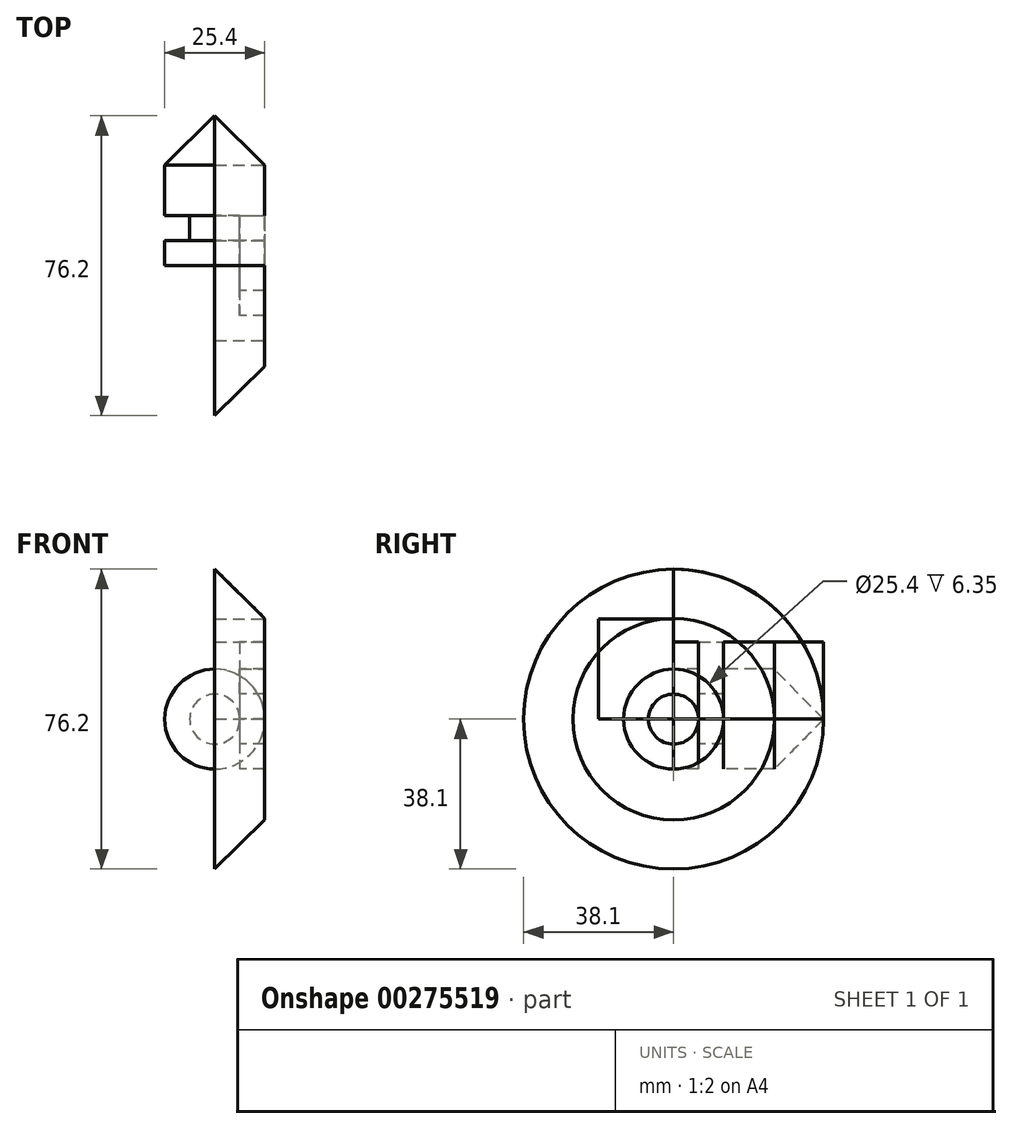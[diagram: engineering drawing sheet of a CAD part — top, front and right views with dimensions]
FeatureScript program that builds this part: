
annotation { "Feature Type Name" : "Feature", "Feature Type Description" : "" }
export const myFeature = defineFeature(function(context is Context, id is Id, definition is map)
    precondition{}
    {
        {
            var Q0;
            Q0=qCreatedBy(makeId("Top.planeOp"),FACE);
            var sketch = newSketch(context, id + "F0", { "sketchPlane" : qUnion([Q0])});
            skLineSegment(sketch, "E0", {"start": v(0, 0) * mm, "end": v(0, 38.1) * mm});
            skLineSegment(sketch, "E1", {"start": v(0, 0) * mm, "end": v(12.7, 0) * mm});
            skLineSegment(sketch, "E2", {"start": v(12.7, 0) * mm, "end": v(12.7, 6.35) * mm});
            skLineSegment(sketch, "E3", {"start": v(12.7, 6.35) * mm, "end": v(6.35, 6.35) * mm});
            skLineSegment(sketch, "E4", {"start": v(6.35, 6.35) * mm, "end": v(6.35, 12.7) * mm});
            skLineSegment(sketch, "E5", {"start": v(6.35, 12.7) * mm, "end": v(12.7, 12.7) * mm});
            skLineSegment(sketch, "E6", {"start": v(12.7, 12.7) * mm, "end": v(12.7, 25.6) * mm});
            skLineSegment(sketch, "E7", {"start": v(12.7, 25.6) * mm, "end": v(0, 38.1) * mm});
            skSolve(sketch);
        }
        {
            var Q0;
            Q0=makeQuery(id+"F0.imprint","IMPRINT",FACE,{"disambiguationData":[TD([[makeQuery(id+"F0.imprint","IMPRINT",EDGE,{"derivedFrom":sQuery(id+"F0.wireOp",EDGE,"E0")}),-1.0]])]});
            extrude(context, id + "F1", {"entities" : qUnion([Q0]), "depth" : 19.56 * mm});
        }
        {
            var Q0;
            Q0=makeQuery(id+"F0.imprint","IMPRINT",FACE,{"disambiguationData":[TD([[makeQuery(id+"F0.imprint","IMPRINT",EDGE,{"derivedFrom":sQuery(id+"F0.wireOp",EDGE,"E0")}),-1.0]])]});
            var Q1;
            Q1=sQuery(id+"F0.wireOp",EDGE,"E0");
            revolve(context, id + "F2", {"entities" : qUnion([Q0]), "axis" : qUnion([Q1]), "revolveType" : RevolveType.FULL});
        }
        {
            var Q0;
            Q0=makeQuery(id+"F0.imprint","IMPRINT",FACE,{"disambiguationData":[TD([[makeQuery(id+"F0.imprint","IMPRINT",EDGE,{"derivedFrom":sQuery(id+"F0.wireOp",EDGE,"E0")}),-1.0]])]});
            var Q1;
            Q1=sQuery(id+"F0.wireOp",EDGE,"E1");
            revolve(context, id + "F3", {"entities" : qUnion([Q0]), "axis" : qUnion([Q1]), "revolveType" : RevolveType.FULL});
        }
        {
            var Q0;
            Q0=qSketchRegion(id+"F0",true);
            var Q1;
            Q1=sQuery(id+"F0.wireOp",EDGE,"E1");
            revolve(context, id + "F4", {"entities" : qUnion([Q0]), "axis" : qUnion([Q1]), "revolveType" : RevolveType.ONE_DIRECTION, "angle" : 90 * degree});
        }
        {
            var Q0;
            Q0=qCreatedBy(makeId("Top.planeOp"),FACE);
            var sketch = newSketch(context, id + "F5", { "sketchPlane" : qUnion([Q0])});
            skLineSegment(sketch, "E8.bottom", {"start": v(0, 0) * mm, "end": v(12.7, 0) * mm});
            skLineSegment(sketch, "E8.top", {"start": v(0, -19.05) * mm, "end": v(12.7, -19.05) * mm});
            skLineSegment(sketch, "E8.left", {"start": v(0, 0) * mm, "end": v(0, -19.05) * mm});
            skLineSegment(sketch, "E8.right", {"start": v(12.7, 0) * mm, "end": v(12.7, -19.05) * mm});
            skSolve(sketch);
        }
        {
            var Q0;
            Q0=makeQuery(id+"F5.imprint","IMPRINT",FACE,{"disambiguationData":[TD([[makeQuery(id+"F5.imprint","IMPRINT",EDGE,{"derivedFrom":sQuery(id+"F5.wireOp",EDGE,"E8.bottom")}),-1.0]])]});
            extrude(context, id + "F6", {"entities" : qUnion([Q0]), "depth" : 25.4 * mm});
        }
    });
